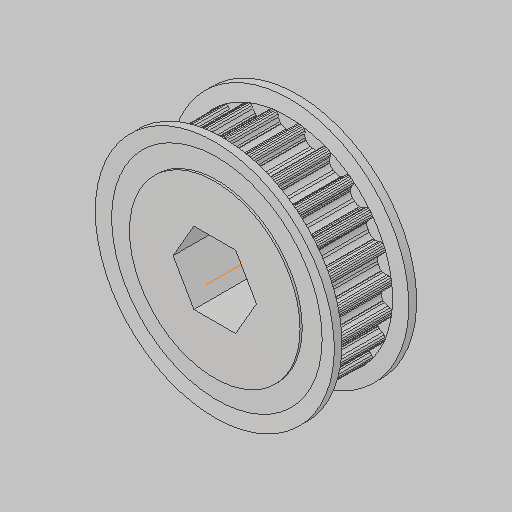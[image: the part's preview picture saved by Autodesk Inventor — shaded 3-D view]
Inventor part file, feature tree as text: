
AUTODESK INVENTOR PART (.ipt)
format: ipt  version: 2023.5 (Build 275446000, 446)  size: 663,552 bytes
history: native  units: in
note: dims shown in document units (in); Inventor stores cm internally (conversion verified against a paired STEP export)
features: mirror x1
ambient origin geometry x8: Origin, YZ Plane, XZ Plane, XY Plane, X Axis, Y Axis, Z Axis, Center Point
bodies: Solid1 (feature_tree)
feature tree (1):
  mirror  "Mirror1"
